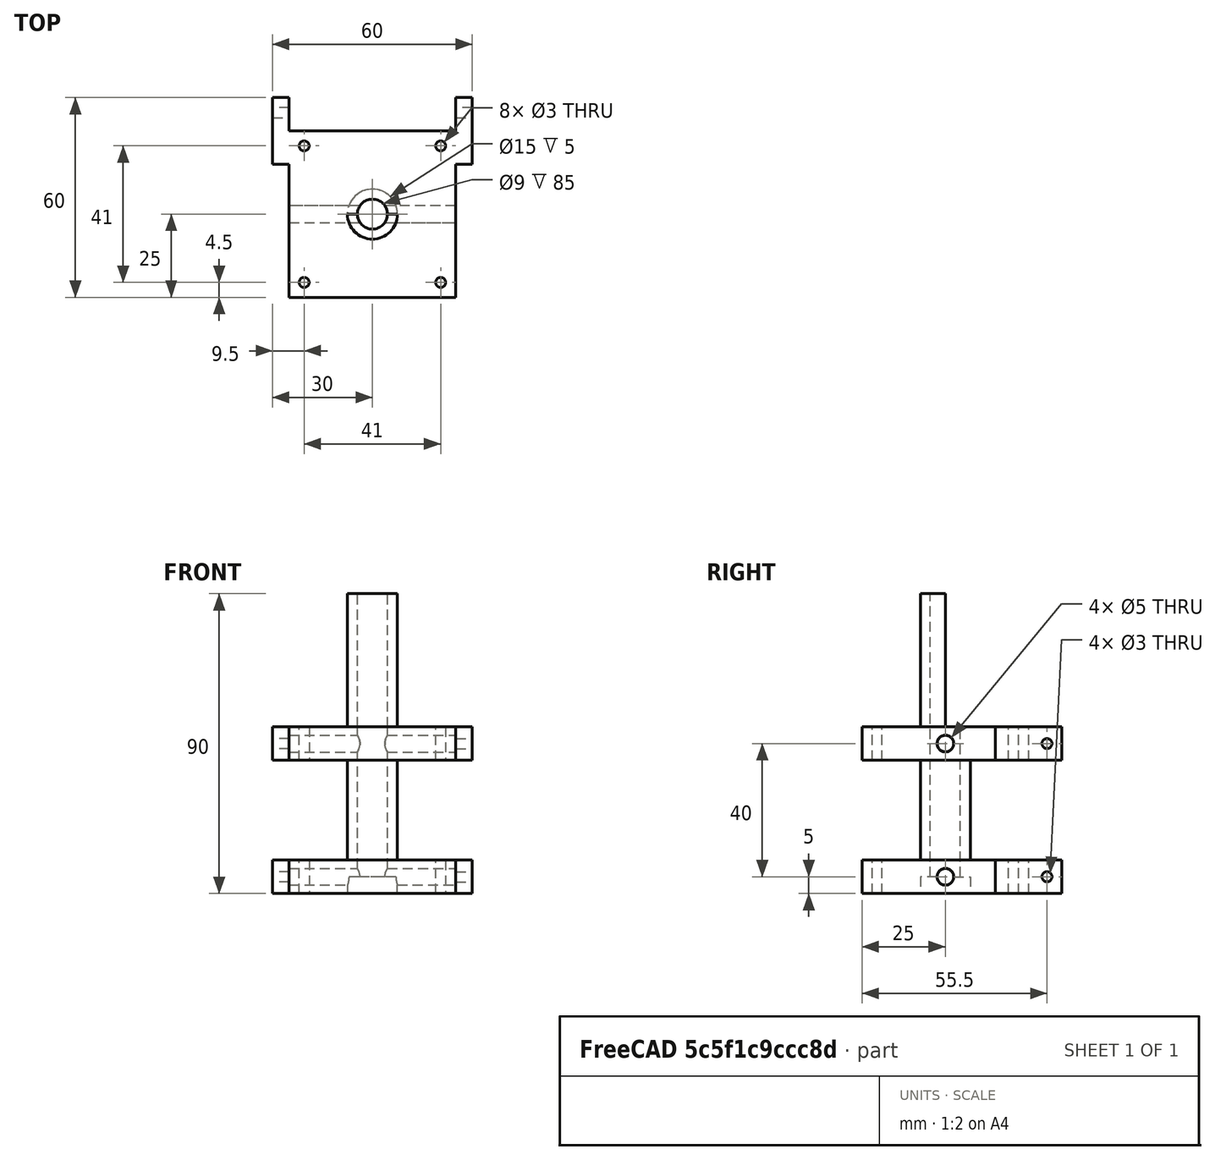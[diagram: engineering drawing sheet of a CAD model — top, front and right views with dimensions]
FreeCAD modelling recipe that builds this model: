
FCSTD DOCUMENT  (FreeCAD 1.0R39109 (Git))
Label: 1st Stage
License: All rights reserved
LicenseURL: https://en.wikipedia.org/wiki/All_rights_reserved
objects: Sketcher::SketchObject×20, PartDesign::Pocket×11, PartDesign::Pad×6, PartDesign::Chamfer×5, PartDesign::Fillet×4, PartDesign::Body×1
note: 119 computed .brp shape members not serialized (recipe doc carries the construction recipe); baked Part::Feature solids carry a one-line shape summary decoded from their .brp

FEATURE [Sketcher::SketchObject] Sketch
  ArcFitTolerance = 1e-06
  AttachmentSupport = -> [XY_Plane]
  FullyConstrained = true
  MakeInternals = false
  MapMode = 5
  sketch-geometry (5):
    g0: LineSegment StartX=-25 StartY=-25 StartZ=0 EndX=25 EndY=-25 EndZ=0
    g1: LineSegment StartX=25 StartY=-25 StartZ=0 EndX=25 EndY=25 EndZ=0
    g2: LineSegment StartX=25 StartY=25 StartZ=0 EndX=-25 EndY=25 EndZ=0
    g3: LineSegment StartX=-25 StartY=25 StartZ=0 EndX=-25 EndY=-25 EndZ=0
    g4: GeomPoint [constr] X=0 Y=0 Z=0
  constraints (12):
    c: Coincident(g0,g1)
    c: Coincident(g1,g2)
    c: Coincident(g2,g3)
    c: Coincident(g3,g0)
    c: Horizontal(g0)
    c: Horizontal(g2)
    c: Vertical(g1)
    c: Vertical(g3)
    c: Symmetric(g2,g0,g4)
    c: Coincident(g4,g-1)
    c: DistanceX(g2,g2) = 50
    c: DistanceY(g1,g1) = 50
FEATURE [PartDesign::Pad] Pad
  Direction = (0,0,1)
  Length = 10
  Length2 = 10
  Profile = -> Sketch
  ReferenceAxis = -> Sketch [N_Axis]
  Refine = true
  Suppressed = false
  Type = 0
FEATURE [Sketcher::SketchObject] Sketch001
  ArcFitTolerance = 1e-06
  AttachmentSupport = -> [Pad]
  FullyConstrained = true
  MakeInternals = false
  MapMode = 5
  Placement = pos=(0,0,10) rot=(0,0,1;0rad)
  sketch-geometry (1):
    g0: Circle CenterX=0 CenterY=0 CenterZ=0 NormalX=0 NormalY=0 NormalZ=1 AngleXU=0 Radius=0
  constraints (2):
    c: Coincident(g0,g-1)
    c: Tangent(g0,g-1)
FEATURE [Sketcher::SketchObject] Sketch002
  ArcFitTolerance = 1e-06
  AttachmentSupport = -> [Pad]
  FullyConstrained = true
  MakeInternals = false
  MapMode = 5
  Placement = pos=(0,0,10) rot=(0,0,1;0rad)
  sketch-geometry (1):
    g0: Circle CenterX=0 CenterY=0 CenterZ=0 NormalX=0 NormalY=0 NormalZ=1 AngleXU=0 Radius=7.5
  constraints (2):
    c: Coincident(g0,g-1)
    c: Diameter(g0) = 15
FEATURE [PartDesign::Pad] Pad001
  BaseFeature = -> Pad
  Direction = (0,0,1)
  Length = 30
  Length2 = 10
  Profile = -> Sketch002
  ReferenceAxis = -> Sketch002 [N_Axis]
  Refine = true
  Suppressed = false
  Type = 0
FEATURE [Sketcher::SketchObject] Sketch003
  ArcFitTolerance = 1e-06
  AttachmentSupport = -> [Pad001]
  FullyConstrained = true
  MakeInternals = false
  MapMode = 5
  Placement = pos=(0,0,40) rot=(0,0,1;0rad)
  sketch-geometry (5):
    g0: LineSegment StartX=-25 StartY=-25 StartZ=0 EndX=25 EndY=-25 EndZ=0
    g1: LineSegment StartX=25 StartY=-25 StartZ=0 EndX=25 EndY=25 EndZ=0
    g2: LineSegment StartX=25 StartY=25 StartZ=0 EndX=-25 EndY=25 EndZ=0
    g3: LineSegment StartX=-25 StartY=25 StartZ=0 EndX=-25 EndY=-25 EndZ=0
    g4: GeomPoint [constr] X=0 Y=0 Z=0
  constraints (12):
    c: Coincident(g0,g1)
    c: Coincident(g1,g2)
    c: Coincident(g2,g3)
    c: Coincident(g3,g0)
    c: Horizontal(g0)
    c: Horizontal(g2)
    c: Vertical(g1)
    c: Vertical(g3)
    c: Symmetric(g2,g0,g4)
    c: Distance(g1,g3) = 50
    c: Distance(g0,g2) = 50
    c: Coincident(g4,g-1)
FEATURE [PartDesign::Pad] Pad002
  BaseFeature = -> Pad001
  Direction = (0,0,1)
  Length = 10
  Length2 = 10
  Profile = -> Sketch003
  ReferenceAxis = -> Sketch003 [N_Axis]
  Refine = true
  Suppressed = false
  Type = 0
FEATURE [Sketcher::SketchObject] Sketch004
  ArcFitTolerance = 1e-06
  AttachmentSupport = -> [Pad002]
  FullyConstrained = true
  MakeInternals = false
  MapMode = 5
  Placement = pos=(0,0,50) rot=(0,0,1;0rad)
  sketch-geometry (1):
    g0: Circle CenterX=0 CenterY=0 CenterZ=0 NormalX=0 NormalY=0 NormalZ=1 AngleXU=0 Radius=4.5
  constraints (2):
    c: Diameter(g0) = 9
    c: Coincident(g0,g-1)
FEATURE [PartDesign::Pocket] Pocket
  BaseFeature = -> Pad002
  Direction = (0,0,-1)
  Length = 50
  Length2 = 5
  Profile = -> Sketch004
  ReferenceAxis = -> Sketch004 [N_Axis]
  Refine = true
  Suppressed = false
  Type = 0
FEATURE [Sketcher::SketchObject] Sketch005
  ArcFitTolerance = 1e-06
  AttachmentSupport = -> [Pocket]
  FullyConstrained = true
  MakeInternals = false
  MapMode = 5
  Placement = pos=(0,0,50) rot=(0,0,1;0rad)
  sketch-geometry (9):
    g0: Circle CenterX=-20.5 CenterY=20.5 CenterZ=0 NormalX=0 NormalY=0 NormalZ=1 AngleXU=0 Radius=1.5
    g1: Circle CenterX=20.5 CenterY=20.5 CenterZ=0 NormalX=0 NormalY=0 NormalZ=1 AngleXU=0 Radius=1.5
    g2: Circle CenterX=20.5 CenterY=-20.5 CenterZ=0 NormalX=0 NormalY=0 NormalZ=1 AngleXU=0 Radius=1.5
    g3: Circle CenterX=-20.5 CenterY=-20.5 CenterZ=0 NormalX=0 NormalY=0 NormalZ=1 AngleXU=0 Radius=1.5
    g4: LineSegment StartX=-25 StartY=-25 StartZ=0 EndX=25 EndY=-25 EndZ=0
    g5: LineSegment StartX=25 StartY=-25 StartZ=0 EndX=25 EndY=25 EndZ=0
    g6: LineSegment StartX=25 StartY=25 StartZ=0 EndX=-25 EndY=25 EndZ=0
    g7: LineSegment StartX=-25 StartY=25 StartZ=0 EndX=-25 EndY=-25 EndZ=0
    g8: GeomPoint [constr] X=0 Y=0 Z=0
  constraints (24):
    c: Diameter(g0) = 3
    c: Diameter(g1) = 3
    c: Diameter(g2) = 3
    c: Diameter(g3) = 3
    c: Coincident(g4,g5)
    c: Coincident(g5,g6)
    c: Coincident(g6,g7)
    c: Coincident(g7,g4)
    c: Horizontal(g4)
    c: Horizontal(g6)
    c: Vertical(g5)
    c: Vertical(g7)
    c: Symmetric(g6,g4,g8)
    c: Distance(g5,g7) = 50
    c: Distance(g4,g6) = 50
    c: Coincident(g8,g-1)
    c: Distance(g0,g6) = 3
    c: Distance(g0,g7) = 3
    c: Distance(g1,g5) = 3
    c: Distance(g1,g6) = 3
    c: Distance(g3,g7) = 3
    c: Distance(g3,g4) = 3
    c: Distance(g2,g4) = 3
    c: Distance(g2,g5) = 3
FEATURE [PartDesign::Pocket] Pocket001
  BaseFeature = -> Pocket
  Direction = (0,0,-1)
  Length = 50
  Length2 = 5
  Profile = -> Sketch005 [Edge2,Edge1,Edge4,Edge3]
  ReferenceAxis = -> Sketch005 [N_Axis]
  Refine = true
  Suppressed = false
  Type = 0
FEATURE [Sketcher::SketchObject] Sketch006
  ArcFitTolerance = 1e-06
  AttachmentSupport = -> [Pocket001]
  FullyConstrained = true
  MakeInternals = false
  MapMode = 5
  Placement = pos=(25,0,0) rot=(0.57735,0.57735,0.57735;2.0944rad)
  sketch-geometry (1):
    g0: Circle CenterX=0 CenterY=5 CenterZ=0 NormalX=0 NormalY=0 NormalZ=1 AngleXU=0 Radius=2.5
  constraints (3):
    c: Diameter(g0) = 5
    c: PointOnObject(g0,g-2)
    c: Distance(g0,g-1) = 2.5
FEATURE [PartDesign::Pocket] Pocket002
  BaseFeature = -> Pocket001
  Direction = (-1,0,0)
  Length = 50
  Length2 = 5
  Profile = -> Sketch006
  ReferenceAxis = -> Sketch006 [N_Axis]
  Refine = true
  Suppressed = false
  Type = 0
FEATURE [Sketcher::SketchObject] Sketch007
  ArcFitTolerance = 1e-06
  AttachmentSupport = -> [Pocket002]
  FullyConstrained = true
  MakeInternals = false
  MapMode = 5
  Placement = pos=(25,0,0) rot=(0.57735,0.57735,0.57735;2.0944rad)
  sketch-geometry (1):
    g0: Circle CenterX=0 CenterY=45 CenterZ=0 NormalX=0 NormalY=0 NormalZ=1 AngleXU=0 Radius=2.5
  constraints (3):
    c: Diameter(g0) = 5
    c: PointOnObject(g0,g-2)
    c: Distance(g0,g-1) = 42.5
FEATURE [PartDesign::Pocket] Pocket003
  BaseFeature = -> Pocket002
  Direction = (-1,0,0)
  Length = 50
  Length2 = 5
  Profile = -> Sketch007
  ReferenceAxis = -> Sketch007 [N_Axis]
  Refine = true
  Suppressed = false
  Type = 0
FEATURE [Sketcher::SketchObject] Sketch008
  ArcFitTolerance = 1e-06
  AttachmentSupport = -> [Pocket003]
  FullyConstrained = true
  MakeInternals = false
  MapMode = 5
  Placement = pos=(0,0,0) rot=(1,0,0;3.14159rad)
FEATURE [Sketcher::SketchObject] Sketch009
  ArcFitTolerance = 1e-06
  AttachmentSupport = -> [Pocket003]
  FullyConstrained = true
  MakeInternals = false
  MapMode = 5
  Placement = pos=(-25,0,0) rot=(0.57735,-0.57735,-0.57735;2.0944rad)
  sketch-geometry (10):
    g0: LineSegment StartX=-35 StartY=0 StartZ=0 EndX=-15 EndY=0 EndZ=0
    g1: LineSegment StartX=-15 StartY=0 StartZ=0 EndX=-15 EndY=10 EndZ=0
    g2: LineSegment StartX=-15 StartY=10 StartZ=0 EndX=-35 EndY=10 EndZ=0
    g3: LineSegment StartX=-35 StartY=10 StartZ=0 EndX=-35 EndY=0 EndZ=0
    g4: GeomPoint [constr] X=-25 Y=5 Z=0
    g5: LineSegment StartX=-35 StartY=40 StartZ=0 EndX=-15 EndY=40 EndZ=0
    g6: LineSegment StartX=-15 StartY=40 StartZ=0 EndX=-15 EndY=50 EndZ=0
    g7: LineSegment StartX=-15 StartY=50 StartZ=0 EndX=-35 EndY=50 EndZ=0
    g8: LineSegment StartX=-35 StartY=50 StartZ=0 EndX=-35 EndY=40 EndZ=0
    g9: GeomPoint [constr] X=-25 Y=45 Z=0
  constraints (26):
    c: Coincident(g0,g1)
    c: Coincident(g1,g2)
    c: Coincident(g2,g3)
    c: Coincident(g3,g0)
    c: Horizontal(g0)
    c: Horizontal(g2)
    c: Vertical(g1)
    c: Vertical(g3)
    c: Symmetric(g2,g0,g4)
    c: Distance(g1,g3) = 20
    c: Distance(g0,g2) = 10
    c: Distance(g-2,g1) = 15
    c: Distance(g4,g-1) = 5
    c: Coincident(g5,g6)
    c: Coincident(g6,g7)
    c: Coincident(g7,g8)
    c: Coincident(g8,g5)
    c: Horizontal(g5)
    c: Horizontal(g7)
    c: Vertical(g6)
    c: Vertical(g8)
    c: Symmetric(g7,g5,g9)
    c: Distance(g6,g8) = 20
    c: Distance(g5,g7) = 10
    c: Distance(g-2,g6) = 15
    c: Distance(g-1,g5) = 40
FEATURE [PartDesign::Pad] Pad003
  BaseFeature = -> Pocket003
  Direction = (-1,0,0)
  Length = 5
  Length2 = 10
  Profile = -> Sketch009
  ReferenceAxis = -> Sketch009 [N_Axis]
  Refine = true
  Suppressed = false
  Type = 0
FEATURE [Sketcher::SketchObject] Sketch010
  ArcFitTolerance = 1e-06
  AttachmentSupport = -> [Pad003]
  FullyConstrained = true
  MakeInternals = false
  MapMode = 5
  Placement = pos=(-30,0,0) rot=(0.57735,-0.57735,-0.57735;2.0944rad)
  sketch-geometry (2):
    g0: Circle CenterX=-30.5 CenterY=5 CenterZ=0 NormalX=0 NormalY=0 NormalZ=1 AngleXU=0 Radius=1.5
    g1: Circle CenterX=-30.5 CenterY=45 CenterZ=0 NormalX=0 NormalY=0 NormalZ=1 AngleXU=0 Radius=1.5
  constraints (6):
    c: Diameter(g0) = 3
    c: Diameter(g1) = 3
    c: Distance(g1,g-2) = 29
    c: DistanceY(g-1,g1) = 45
    c: DistanceY(g-1,g0) = 5
    c: Distance(g0,g-2) = 29
FEATURE [PartDesign::Pocket] Pocket004
  BaseFeature = -> Pad003
  Direction = (1,0,0)
  Length = 5
  Length2 = 5
  Profile = -> Sketch010
  ReferenceAxis = -> Sketch010 [N_Axis]
  Refine = true
  Suppressed = false
  Type = 0
FEATURE [Sketcher::SketchObject] Sketch011
  ArcFitTolerance = 1e-06
  AttachmentSupport = -> [Pocket004]
  FullyConstrained = true
  MakeInternals = false
  MapMode = 5
  Placement = pos=(25,0,0) rot=(0.57735,0.57735,0.57735;2.0944rad)
  sketch-geometry (10):
    g0: LineSegment StartX=15 StartY=0 StartZ=0 EndX=35 EndY=0 EndZ=0
    g1: LineSegment StartX=35 StartY=0 StartZ=0 EndX=35 EndY=10 EndZ=0
    g2: LineSegment StartX=35 StartY=10 StartZ=0 EndX=15 EndY=10 EndZ=0
    g3: LineSegment StartX=15 StartY=10 StartZ=0 EndX=15 EndY=0 EndZ=0
    g4: GeomPoint [constr] X=25 Y=5 Z=0
    g5: LineSegment StartX=15 StartY=40 StartZ=0 EndX=35 EndY=40 EndZ=0
    g6: LineSegment StartX=35 StartY=40 StartZ=0 EndX=35 EndY=50 EndZ=0
    g7: LineSegment StartX=35 StartY=50 StartZ=0 EndX=15 EndY=50 EndZ=0
    g8: LineSegment StartX=15 StartY=50 StartZ=0 EndX=15 EndY=40 EndZ=0
    g9: GeomPoint [constr] X=25 Y=45 Z=0
  constraints (26):
    c: Coincident(g0,g1)
    c: Coincident(g1,g2)
    c: Coincident(g2,g3)
    c: Coincident(g3,g0)
    c: Horizontal(g0)
    c: Horizontal(g2)
    c: Vertical(g1)
    c: Vertical(g3)
    c: Symmetric(g2,g0,g4)
    c: Distance(g1,g3) = 20
    c: Distance(g0,g2) = 10
    c: Coincident(g5,g6)
    c: Coincident(g6,g7)
    c: Coincident(g7,g8)
    c: Coincident(g8,g5)
    c: Horizontal(g5)
    c: Horizontal(g7)
    c: Vertical(g6)
    c: Vertical(g8)
    c: Symmetric(g7,g5,g9)
    c: Distance(g6,g8) = 20
    c: Distance(g5,g7) = 10
    c: Distance(g4,g-2) = 25
    c: Distance(g-1,g2) = 10
    c: Distance(g-2,g8) = 15
    c: Distance(g-1,g5) = 40
FEATURE [PartDesign::Pad] Pad004
  BaseFeature = -> Pocket004
  Direction = (1,0,0)
  Length = 5
  Length2 = 10
  Profile = -> Sketch011
  ReferenceAxis = -> Sketch011 [N_Axis]
  Refine = true
  Suppressed = false
  Type = 0
FEATURE [Sketcher::SketchObject] Sketch012
  ArcFitTolerance = 1e-06
  AttachmentSupport = -> [Pad004]
  FullyConstrained = true
  MakeInternals = false
  MapMode = 5
  Placement = pos=(30,0,0) rot=(0.57735,0.57735,0.57735;2.0944rad)
  sketch-geometry (2):
    g0: Circle CenterX=30.5 CenterY=5 CenterZ=0 NormalX=0 NormalY=0 NormalZ=1 AngleXU=0 Radius=1.5
    g1: Circle CenterX=30.5 CenterY=45 CenterZ=0 NormalX=0 NormalY=0 NormalZ=1 AngleXU=0 Radius=1.5
  constraints (6):
    c: Diameter(g0) = 3
    c: Diameter(g1) = 3
    c: Distance(g1,g-2) = 29
    c: DistanceY(g-1,g1) = 45
    c: Distance(g0,g-1) = 5
    c: Distance(g0,g-2) = 29
FEATURE [PartDesign::Pocket] Pocket005
  BaseFeature = -> Pad004
  Direction = (-1,0,0)
  Length = 5
  Length2 = 5
  Profile = -> Sketch012
  ReferenceAxis = -> Sketch012 [N_Axis]
  Refine = true
  Suppressed = false
  Type = 0
FEATURE [Sketcher::SketchObject] Sketch013
  ArcFitTolerance = 1e-06
  AttachmentSupport = -> [Pocket005]
  FullyConstrained = true
  MakeInternals = false
  MapMode = 5
  Placement = pos=(0,0,0) rot=(1,0,0;3.14159rad)
  sketch-geometry (1):
    g0: Circle CenterX=0 CenterY=0 CenterZ=0 NormalX=0 NormalY=0 NormalZ=1 AngleXU=0 Radius=7.5
  constraints (2):
    c: Diameter(g0) = 15
    c: Coincident(g0,g-1)
FEATURE [PartDesign::Pocket] Pocket006
  BaseFeature = -> Pocket005
  Direction = (0,0,1)
  Length = 5
  Length2 = 5
  Profile = -> Sketch013
  ReferenceAxis = -> Sketch013 [N_Axis]
  Refine = true
  Suppressed = false
  Type = 0
FEATURE [Sketcher::SketchObject] Sketch014
  ArcFitTolerance = 1e-06
  AttachmentSupport = -> [Pocket006]
  FullyConstrained = true
  MakeInternals = false
  MapMode = 5
  Placement = pos=(0,0,50) rot=(0,0,1;0rad)
  sketch-geometry (1):
    g0: Circle CenterX=0 CenterY=0 CenterZ=0 NormalX=0 NormalY=0 NormalZ=1 AngleXU=0 Radius=7.5
  constraints (2):
    c: Diameter(g0) = 15
    c: Coincident(g0,g-1)
FEATURE [PartDesign::Pad] Pad005
  BaseFeature = -> Pocket006
  Direction = (0,0,1)
  Length = 40
  Length2 = 10
  Profile = -> Sketch014
  ReferenceAxis = -> Sketch014 [N_Axis]
  Refine = true
  Suppressed = false
  Type = 0
FEATURE [Sketcher::SketchObject] Sketch015
  ArcFitTolerance = 1e-06
  AttachmentSupport = -> [Pad005]
  FullyConstrained = true
  MakeInternals = false
  MapMode = 5
  Placement = pos=(0,0,90) rot=(0,0,1;0rad)
  sketch-geometry (1):
    g0: Circle CenterX=0 CenterY=0 CenterZ=0 NormalX=0 NormalY=0 NormalZ=1 AngleXU=0 Radius=4.5
  constraints (2):
    c: Diameter(g0) = 9
    c: Coincident(g0,g-1)
FEATURE [PartDesign::Pocket] Pocket007
  BaseFeature = -> Pad005
  Direction = (0,0,-1)
  Length = 40
  Length2 = 5
  Profile = -> Sketch015
  ReferenceAxis = -> Sketch015 [N_Axis]
  Refine = true
  Suppressed = false
  Type = 0
FEATURE [Sketcher::SketchObject] Sketch016
  ArcFitTolerance = 1e-06
  AttachmentSupport = -> [Pocket007]
  FullyConstrained = true
  MakeInternals = false
  MapMode = 5
  Placement = pos=(0,0,90) rot=(0,0,1;0rad)
  sketch-geometry (4):
    g0: LineSegment StartX=-7.5 StartY=8 StartZ=0 EndX=-7.5 EndY=0 EndZ=0
    g1: LineSegment StartX=-7.5 StartY=0 StartZ=0 EndX=7.5 EndY=0 EndZ=0
    g2: LineSegment StartX=7.5 StartY=0 StartZ=0 EndX=7.5 EndY=8 EndZ=0
    g3: LineSegment StartX=7.5 StartY=8 StartZ=0 EndX=-7.5 EndY=8 EndZ=0
  constraints (12):
    c: Coincident(g0,g1)
    c: Coincident(g1,g2)
    c: Coincident(g2,g3)
    c: Coincident(g3,g0)
    c: Vertical(g0)
    c: Vertical(g2)
    c: Horizontal(g1)
    c: Horizontal(g3)
    c: Distance(g0,g2) = 15
    c: Distance(g1,g3) = 8
    c: Distance(g-1,g3) = 8
    c: Distance(g-2,g0) = 7.5
FEATURE [PartDesign::Pocket] Pocket008
  BaseFeature = -> Pocket007
  Direction = (0,0,-1)
  Length = 40
  Length2 = 5
  Profile = -> Sketch016
  ReferenceAxis = -> Sketch016 [N_Axis]
  Refine = true
  Suppressed = false
  Type = 0
FEATURE [Sketcher::SketchObject] Sketch017
  ArcFitTolerance = 1e-06
  AttachmentSupport = -> [Pocket008]
  FullyConstrained = true
  MakeInternals = false
  MapMode = 5
  Placement = pos=(0,0,90) rot=(0,0,1;0rad)
FEATURE [PartDesign::Fillet] Fillet
  Base = -> Pocket008 [Face32]
  BaseFeature = -> Pocket008
  Radius = 1
  Refine = true
  SupportTransform = false
  Suppressed = false
  UseAllEdges = false
FEATURE [PartDesign::Chamfer] Chamfer
  Angle = 45
  Base = -> Pocket008 [Edge124,Edge56,Edge139,Edge58]
  BaseFeature = -> Pocket008
  ChamferType = 0
  FlipDirection = false
  Refine = true
  Size = 1
  Size2 = 1
  SupportTransform = false
  Suppressed = false
  UseAllEdges = false
FEATURE [PartDesign::Chamfer] Chamfer001
  Angle = 45
  Base = -> Chamfer [Edge144,Edge142,Edge138,Edge140,Edge41,Vertex35,Edge40,Edge39,Edge38,Edge94,Edge96,Edge97,Edge95,Edge22,Edge23,Edge20,Edge19]
  BaseFeature = -> Chamfer
  ChamferType = 0
  FlipDirection = false
  Refine = true
  Size = 1
  Size2 = 1
  SupportTransform = false
  Suppressed = false
  UseAllEdges = false
FEATURE [PartDesign::Chamfer] Chamfer002
  Angle = 45
  Base = -> Chamfer001 [Edge157,Edge30]
  BaseFeature = -> Chamfer001
  ChamferType = 0
  FlipDirection = false
  Refine = true
  Size = 4.5
  Size2 = 1
  SupportTransform = false
  Suppressed = false
  UseAllEdges = false
FEATURE [PartDesign::Chamfer] Chamfer003
  Angle = 45
  Base = -> Chamfer002 [Edge168,Edge41]
  BaseFeature = -> Chamfer002
  ChamferType = 0
  FlipDirection = false
  Refine = true
  Size = 4.5
  Size2 = 1
  SupportTransform = false
  Suppressed = false
  UseAllEdges = false
FEATURE [PartDesign::Fillet] Fillet001
  Base = -> Chamfer003 [Edge50]
  BaseFeature = -> Chamfer003
  Radius = 2
  Refine = true
  SupportTransform = false
  Suppressed = false
  UseAllEdges = false
FEATURE [PartDesign::Fillet] Fillet002
  Base = -> Fillet001 [Edge181]
  BaseFeature = -> Fillet001
  Radius = 2
  Refine = true
  SupportTransform = false
  Suppressed = false
  UseAllEdges = false
FEATURE [PartDesign::Fillet] Fillet003
  Base = -> Fillet002 [Edge162,Edge50]
  BaseFeature = -> Fillet002
  Radius = 1.99
  Refine = true
  SupportTransform = false
  Suppressed = false
  UseAllEdges = false
FEATURE [Sketcher::SketchObject] Sketch018
  ArcFitTolerance = 1e-06
  AttachmentSupport = -> [Fillet003]
  FullyConstrained = true
  MakeInternals = false
  MapMode = 5
  Placement = pos=(0,0,90) rot=(0,0,1;0rad)
  sketch-geometry (1):
    g0: Circle CenterX=0 CenterY=0 CenterZ=0 NormalX=0 NormalY=0 NormalZ=1 AngleXU=0 Radius=7.5
  constraints (2):
    c: Coincident(g0,g-1)
    c: Diameter(g0) = 15
FEATURE [PartDesign::Pocket] Pocket009
  BaseFeature = -> Fillet003
  Direction = (0,0,-1)
  Length = 40
  Length2 = 5
  Profile = -> Sketch018 [Edge1]
  ReferenceAxis = -> Sketch018 [N_Axis]
  Refine = true
  Suppressed = false
  Type = 0
FEATURE [PartDesign::Chamfer] Chamfer004
  Angle = 45
  Base = -> Pocket009 [Edge161,Edge56,Edge46,Edge151]
  BaseFeature = -> Pocket009
  ChamferType = 0
  FlipDirection = false
  Refine = true
  Size = 1
  Size2 = 1
  SupportTransform = false
  Suppressed = false
  UseAllEdges = false
FEATURE [Sketcher::SketchObject] Sketch019
  ArcFitTolerance = 1e-06
  AttachmentSupport = -> [Chamfer004]
  FullyConstrained = true
  MakeInternals = false
  MapMode = 5
  Placement = pos=(0,0,10) rot=(0,0,1;0rad)
  sketch-geometry (5):
    g0: LineSegment StartX=-1 StartY=-25 StartZ=0 EndX=1 EndY=-25 EndZ=0
    g1: LineSegment StartX=1 StartY=-25 StartZ=0 EndX=1 EndY=-7.5 EndZ=0
    g2: LineSegment StartX=1 StartY=-7.5 StartZ=0 EndX=-1 EndY=-7.5 EndZ=0
    g3: LineSegment StartX=-1 StartY=-7.5 StartZ=0 EndX=-1 EndY=-25 EndZ=0
    g4: GeomPoint [constr] X=0 Y=-16.25 Z=0
  constraints (13):
    c: Coincident(g0,g1)
    c: Coincident(g1,g2)
    c: Coincident(g2,g3)
    c: Coincident(g3,g0)
    c: Horizontal(g0)
    c: Horizontal(g2)
    c: Vertical(g1)
    c: Vertical(g3)
    c: Symmetric(g2,g0,g4)
    c: Distance(g1,g3) = 2
    c: Distance(g0,g2) = 17.5
    c: PointOnObject(g4,g-2)
    c: Distance(g-1,g0) = 25
FEATURE [PartDesign::Pocket] Pocket010
  BaseFeature = -> Chamfer004
  Direction = (0,0,-1)
  Length = 2
  Length2 = 5
  Profile = -> Sketch019
  ReferenceAxis = -> Sketch019 [N_Axis]
  Refine = true
  Suppressed = false
  Type = 0
FEATURE [PartDesign::Body] Body  label="Körper"
  AllowCompound = false
  Group = -> [Sketch,Pad,Sketch001,Sketch002,Pad001,Sketch003,Pad002,Sketch004,Pocket,Sketch005,Pocket001,Sketch006,Pocket002,Sketch007,Pocket003,Sketch008,Sketch009,Pad003,Sketch010,Pocket004,Sketch011,Pad004,Sketch012,Pocket005,Sketch013,Pocket006,Sketch014,Pad005,Sketch015,Pocket007,Sketch016,Pocket008,Sketch017,Fillet,Chamfer,Chamfer001,Chamfer002,Chamfer003,Fillet001,Fillet002,Fillet003,Sketch018,+4 more]
  Origin = -> Origin
  Tip = -> Pocket010
